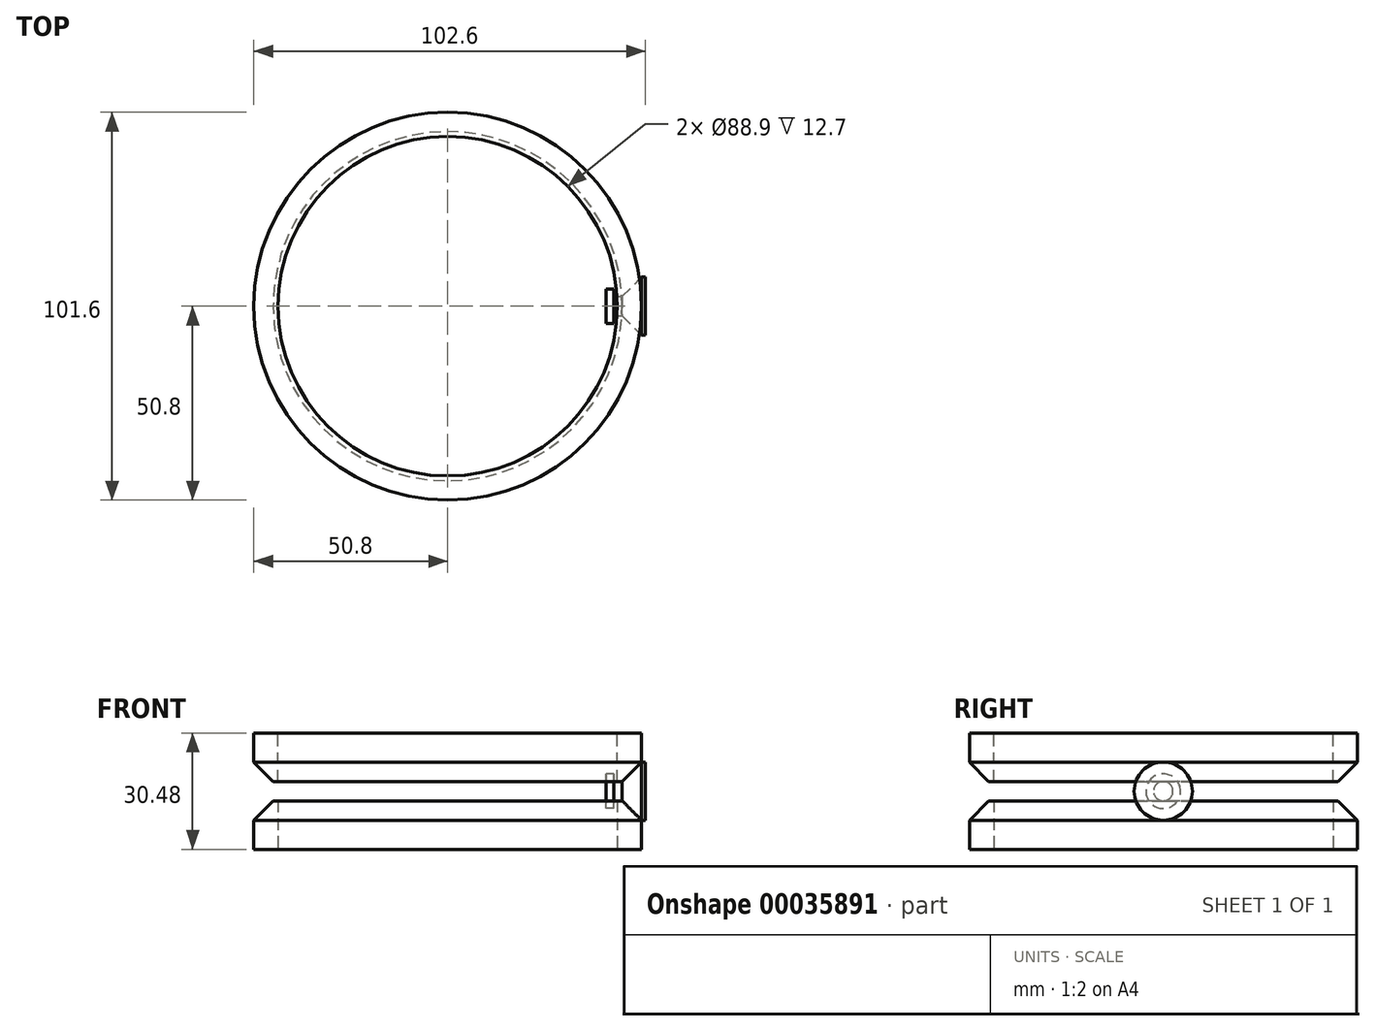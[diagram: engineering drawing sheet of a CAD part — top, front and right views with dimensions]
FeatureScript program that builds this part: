
annotation { "Feature Type Name" : "Feature", "Feature Type Description" : "" }
export const myFeature = defineFeature(function(context is Context, id is Id, definition is map)
    precondition{}
    {
        {
            var Q0;
            Q0=qCreatedBy(makeId("Top.planeOp"),FACE);
            var sketch = newSketch(context, id + "F0", { "sketchPlane" : qUnion([Q0])});
            skCircle(sketch, "E0", {"center": v(0, 0) * mm, "radius": 50.8 * mm});
            skCircle(sketch, "E1", {"center": v(0, 0) * mm, "radius": 44.45 * mm});
            skSolve(sketch);
        }
        {
            var Q0;
            Q0 = qSketchRegion(id + "F0", true);
            extrude(context, id + "F1", {"entities" : qUnion([Q0]), "depth" : 12.7 * mm});
        }
        {
            var Q0;
            Q0=makeQuery(id+"F1.opExtrude","CAP_EDGE",EDGE,{"disambiguationData":[OSD([sQuery(id+"F0.wireOp",EDGE,"E0")])],"isStart":false});
            chamfer(context, id + "F2", {"entities" : qUnion([Q0]), "width" : 5.08 * mm, "tangentPropagation" : true});
        }
        {
            var Q0;
            Q0=qCreatedBy(makeId("Right.planeOp"),FACE);
            cPlane(context, id + "F3", {"entities" : qUnion([Q0]), "cplaneType" : CPlaneType.OFFSET, "offset" : 50.8 * mm, "width" : 152.4 * mm, "height" : 152.4 * mm});
        }
        {
            var Q0;
            Q0=qCreatedBy(id+"F3.planeOp",FACE);
            var sketch = newSketch(context, id + "F4", { "sketchPlane" : qUnion([Q0])});
            skCircle(sketch, "E2", {"center": v(0, 15.24) * mm, "radius": 7.62 * mm});
            skSolve(sketch);
        }
        {
            var Q0;
            Q0 = qSketchRegion(id + "F4", true);
            extrude(context, id + "F5", {"entities" : qUnion([Q0]), "oppositeDirection" : true, "depth" : 5.08 * mm});
        }
        {
            var Q0;
            Q0=makeQuery(id+"F5.opExtrude","CAP_EDGE",EDGE,{"disambiguationData":[OSD([sQuery(id+"F4.wireOp",EDGE,"E2")])],"isStart":false});
            chamfer(context, id + "F6", {"entities" : qUnion([Q0]), "width" : 5.08 * mm, "tangentPropagation" : true});
        }
        {
            var Q0;
            Q0=makeQuery(id+"F5.opExtrude","CAP_FACE",FACE,{"disambiguationData":[OSD([sQuery(id+"F4.wireOp",EDGE,"E2")])],"isStart":false});
            extrude(context, id + "F7", {"entities" : qUnion([Q0]), "operationType" : NewBodyOperationType.ADD, "depth" : 3.17 * mm});
        }
        {
            var Q0;
            Q0=makeQuery(id+"F1.opExtrude","CAP_FACE",FACE,{"disambiguationData":[OSD([sQuery(id+"F0.wireOp",EDGE,"E0"),sQuery(id+"F0.wireOp",EDGE,"E1")])],"isStart":false});
            cPlane(context, id + "F8", {"entities" : qUnion([Q0]), "cplaneType" : CPlaneType.OFFSET, "offset" : 2.54 * mm, "width" : 152.4 * mm, "height" : 152.4 * mm});
        }
        {
            var Q0;
            Q0=makeQuery(id+"F1.opExtrude","SWEPT_BODY",BODY,{"disambiguationData":[OSD([sQuery(id+"F0.wireOp",EDGE,"E0"),sQuery(id+"F0.wireOp",EDGE,"E1")])]});
            var Q1;
            Q1=qCreatedBy(id+"F8.planeOp",FACE);
            mirror(context, id + "F9", {"entities" : qUnion([Q0]), "mirrorPlane" : qUnion([Q1])});
        }
        {
            var Q0;
            Q0=makeQuery(id+"F7.opExtrude","CAP_FACE",FACE,{"disambiguationData":[OSD([sQuery(id+"F4.wireOp",EDGE,"E2")])],"isStart":false});
            var sketch = newSketch(context, id + "F10", { "sketchPlane" : qUnion([Q0])});
            skCircle(sketch, "E3.0", {"center": v(0, 15.24) * mm, "radius": 2.54 * mm});
            skCircle(sketch, "E4", {"center": v(0, 15.24) * mm, "radius": 4.54 * mm});
            skSolve(sketch);
        }
        {
            var Q0;
            Q0 = qSketchRegion(id + "F10", true);
            extrude(context, id + "F11", {"entities" : qUnion([Q0]), "operationType" : NewBodyOperationType.ADD, "oppositeDirection" : true, "depth" : 1 * mm});
        }
        {
            var Q0;
            Q0=makeQuery(id+"F11.boolean.opBoolean","MERGE",FACE,{"derivedFrom":[makeQuery(id+"F7.opExtrude","CAP_FACE",FACE,{"disambiguationData":[OSD([sQuery(id+"F4.wireOp",EDGE,"E2")])],"isStart":false}),makeQuery(id+"F11.opExtrude","CAP_FACE",FACE,{"disambiguationData":[OSD([sQuery(id+"F10.wireOp",EDGE,"E3.0"),sQuery(id+"F10.wireOp",EDGE,"E4")])],"isStart":true})]});
            extrude(context, id + "F12", {"entities" : qUnion([Q0]), "operationType" : NewBodyOperationType.ADD, "depth" : 1 * mm});
        }
        {
            var Q0;
            Q0=makeQuery(id+"F5.opExtrude","CAP_FACE",FACE,{"disambiguationData":[OSD([sQuery(id+"F4.wireOp",EDGE,"E2")])],"isStart":true});
            extrude(context, id + "F13", {"entities" : qUnion([Q0]), "operationType" : NewBodyOperationType.ADD, "depth" : 1 * mm});
        }
    });
